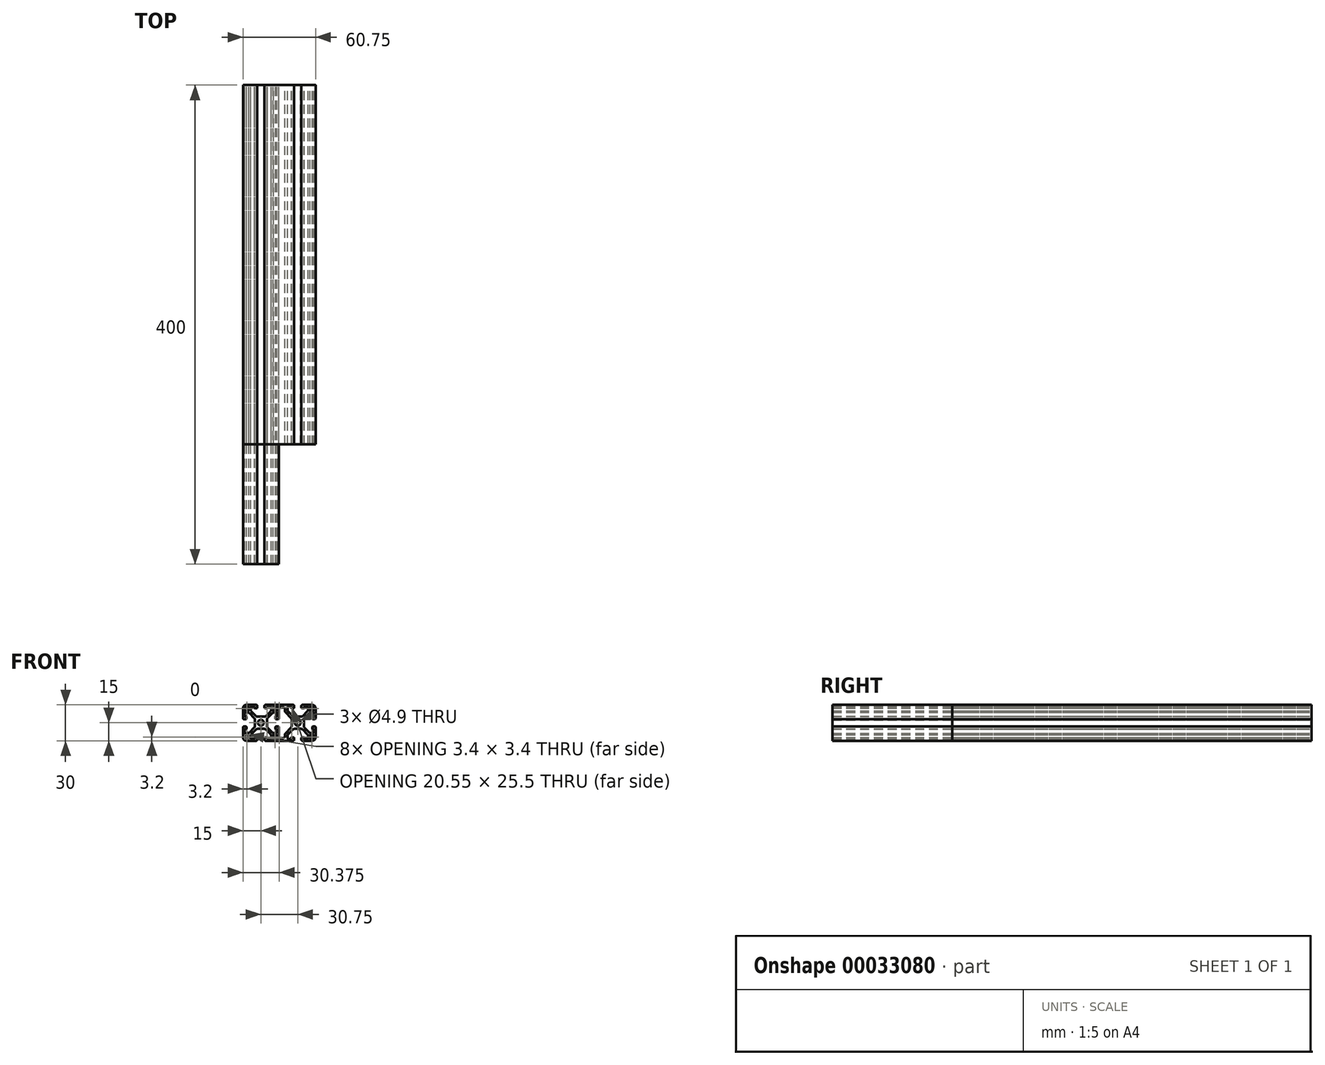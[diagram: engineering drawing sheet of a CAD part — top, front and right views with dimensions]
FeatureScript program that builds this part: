
annotation { "Feature Type Name" : "Feature", "Feature Type Description" : "" }
export const myFeature = defineFeature(function(context is Context, id is Id, definition is map)
    precondition{}
    {
        {
            var Q0;
            Q0=qCreatedBy(makeId("Front.planeOp"),FACE);
            var sketch = newSketch(context, id + "F0", { "sketchPlane" : qUnion([Q0])});
            skLineSegment(sketch, "E0.rect.bottom", {"start": v(-12, 15) * mm, "end": v(-4, 15) * mm});
            skLineSegment(sketch, "E0.rect.top", {"start": v(-12, -15) * mm, "end": v(-4, -15) * mm});
            skLineSegment(sketch, "E0.rect.left", {"start": v(-15, 12) * mm, "end": v(-15, 4) * mm});
            skLineSegment(sketch, "E0.rect.right", {"start": v(15, 12.1) * mm, "end": v(15, 4) * mm});
            skPoint(sketch, "E0.rect.middle", {"position": v(0, 0) * mm});
            skCircle(sketch, "E1", {"center": v(0, 0) * mm, "radius": 2.45 * mm});
            skLineSegment(sketch, "E2", {"start": v(-19.66, 12.1) * mm, "end": v(17.2, 12.1) * mm, "construction": true});
            skLineSegment(sketch, "E3", {"start": v(-19.97, 5.1) * mm, "end": v(17.59, 5.1) * mm, "construction": true});
            skLineSegment(sketch, "E4.rect.bottom", {"start": v(-3, 17.9) * mm, "end": v(3, 17.9) * mm, "construction": true});
            skLineSegment(sketch, "E4.rect.left", {"start": v(-3, 14) * mm, "end": v(-3, 12.85) * mm});
            skPoint(sketch, "E4.rect.middle", {"position": v(0, 15) * mm});
            skLineSegment(sketch, "E5", {"start": v(15, 15) * mm, "end": v(-15, -15) * mm, "construction": true});
            skLineSegment(sketch, "E6", {"start": v(-15, 15) * mm, "end": v(15, -15) * mm, "construction": true});
            skLineSegment(sketch, "E7", {"start": v(-9.23, 9.23) * mm, "end": v(-6.55, 6.55) * mm});
            skLineSegment(sketch, "E8", {"start": v(5.83, 5.83) * mm, "end": v(8.5, 8.5) * mm});
            skLineSegment(sketch, "E9.trimOffspring", {"start": v(4, 15) * mm, "end": v(12, 15) * mm});
            skArc(sketch, "E10.filletArc", {"start": v(-3, 14) * mm, "mid": v(-3.3, 14.7) * mm, "end": v(-4, 15) * mm});
            skPoint(sketch, "E11.visualSharp", {"position": v(8.57, 8.57) * mm});
            skPoint(sketch, "E12.visualSharp", {"position": v(-10.1, 10.1) * mm});
            skPoint(sketch, "E13.visualSharp", {"position": v(-5.1, 5.1) * mm});
            skPoint(sketch, "E14.visualSharp", {"position": v(5.1, 5.1) * mm});
            skPoint(sketch, "E15.visualSharp", {"position": v(-3, 12.1) * mm});
            skPoint(sketch, "E16.visualSharp", {"position": v(-15, 15) * mm});
            skArc(sketch, "E16.filletArc", {"start": v(-12, 15) * mm, "mid": v(-14.12, 14.12) * mm, "end": v(-15, 12) * mm});
            skPoint(sketch, "E17.MirrorP", {"position": v(10.93, 10.93) * mm});
            skPoint(sketch, "E18.MirrorP", {"position": v(10.93, 13.67) * mm});
            skPoint(sketch, "E19.MirrorP", {"position": v(13.67, 13.67) * mm});
            skPoint(sketch, "E20.MirrorP", {"position": v(13.67, 10.93) * mm});
            skPoint(sketch, "E21.newPointA", {"position": v(-3.65, 5.1) * mm});
            skPoint(sketch, "E21.newPointB", {"position": v(-5.45, 5.1) * mm});
            skLineSegment(sketch, "E22.MirrorCS", {"start": v(3, 14) * mm, "end": v(3, 12.85) * mm});
            skArc(sketch, "E23.MirrorCS", {"start": v(3, 14) * mm, "mid": v(3.3, 14.7) * mm, "end": v(4, 15) * mm});
            skLineSegment(sketch, "E24.MirrorCS", {"start": v(12, 15) * mm, "end": v(4, 15) * mm});
            skArc(sketch, "E25.MirrorCS", {"start": v(12, 15) * mm, "mid": v(14.12, 14.12) * mm, "end": v(15, 12) * mm});
            skLineSegment(sketch, "E26", {"start": v(-5.4, 13.3) * mm, "end": v(-5.4, 12.3) * mm});
            skLineSegment(sketch, "E27", {"start": v(-5.2, 12.1) * mm, "end": v(-3.75, 12.1) * mm});
            skLineSegment(sketch, "E28", {"start": v(-7.87, 9.28) * mm, "end": v(-4.42, 5.83) * mm});
            skLineSegment(sketch, "E29", {"start": v(-8.6, 11.05) * mm, "end": v(-8.6, 12.75) * mm});
            skLineSegment(sketch, "E30", {"start": v(-7.85, 13.5) * mm, "end": v(-5.6, 13.5) * mm});
            skPoint(sketch, "E31.visualSharp", {"position": v(-8.6, 10.01) * mm});
            skArc(sketch, "E31.filletArc", {"start": v(-8.6, 11.05) * mm, "mid": v(-8.4, 10.1) * mm, "end": v(-7.87, 9.28) * mm});
            skLineSegment(sketch, "E32", {"start": v(-2.65, 5.1) * mm, "end": v(0, 5.1) * mm});
            skPoint(sketch, "E33.newPointA", {"position": v(-3.69, 5.1) * mm});
            skArc(sketch, "E33.filletArc", {"start": v(-4.42, 5.83) * mm, "mid": v(-3.6, 5.3) * mm, "end": v(-2.65, 5.1) * mm});
            skPoint(sketch, "E34.visualSharp", {"position": v(-8.6, 13.5) * mm});
            skArc(sketch, "E34.filletArc", {"start": v(-7.85, 13.5) * mm, "mid": v(-8.38, 13.28) * mm, "end": v(-8.6, 12.75) * mm});
            skArc(sketch, "E35.filletArc", {"start": v(-3.75, 12.1) * mm, "mid": v(-3.22, 12.32) * mm, "end": v(-3, 12.85) * mm});
            skPoint(sketch, "E36.visualSharp", {"position": v(-5.4, 13.5) * mm});
            skArc(sketch, "E36.filletArc", {"start": v(-5.4, 13.3) * mm, "mid": v(-5.46, 13.44) * mm, "end": v(-5.6, 13.5) * mm});
            skPoint(sketch, "E37.visualSharp", {"position": v(-5.4, 12.1) * mm});
            skArc(sketch, "E37.filletArc", {"start": v(-5.4, 12.3) * mm, "mid": v(-5.34, 12.16) * mm, "end": v(-5.2, 12.1) * mm});
            skLineSegment(sketch, "E38.MirrorCS", {"start": v(2.65, 5.1) * mm, "end": v(0, 5.1) * mm});
            skArc(sketch, "E39.MirrorCS", {"start": v(4.42, 5.83) * mm, "mid": v(3.6, 5.3) * mm, "end": v(2.65, 5.1) * mm});
            skLineSegment(sketch, "E40.MirrorCS", {"start": v(7.87, 9.28) * mm, "end": v(4.42, 5.83) * mm});
            skArc(sketch, "E41.MirrorCS", {"start": v(8.6, 11.05) * mm, "mid": v(8.4, 10.1) * mm, "end": v(7.87, 9.28) * mm});
            skLineSegment(sketch, "E42.MirrorCS", {"start": v(8.6, 11.05) * mm, "end": v(8.6, 12.75) * mm});
            skArc(sketch, "E43.MirrorCS", {"start": v(7.85, 13.5) * mm, "mid": v(8.38, 13.28) * mm, "end": v(8.6, 12.75) * mm});
            skLineSegment(sketch, "E44.MirrorCS", {"start": v(7.85, 13.5) * mm, "end": v(5.6, 13.5) * mm});
            skArc(sketch, "E45.MirrorCS", {"start": v(5.4, 13.3) * mm, "mid": v(5.46, 13.44) * mm, "end": v(5.6, 13.5) * mm});
            skLineSegment(sketch, "E46.MirrorCS", {"start": v(5.4, 13.3) * mm, "end": v(5.4, 12.3) * mm});
            skArc(sketch, "E47.MirrorCS", {"start": v(5.4, 12.3) * mm, "mid": v(5.34, 12.16) * mm, "end": v(5.2, 12.1) * mm});
            skLineSegment(sketch, "E48.MirrorCS", {"start": v(5.2, 12.1) * mm, "end": v(3.75, 12.1) * mm});
            skArc(sketch, "E49.MirrorCS", {"start": v(3.75, 12.1) * mm, "mid": v(3.22, 12.32) * mm, "end": v(3, 12.85) * mm});
            skPoint(sketch, "E50.orphan", {"position": v(3, 12.1) * mm});
            skArc(sketch, "E51.MirrorCS", {"start": v(-3, -14) * mm, "mid": v(-3.3, -14.7) * mm, "end": v(-4, -15) * mm});
            skLineSegment(sketch, "E52.MirrorCS", {"start": v(-3, -14) * mm, "end": v(-3, -12.85) * mm});
            skArc(sketch, "E53.MirrorCS", {"start": v(-3.75, -12.1) * mm, "mid": v(-3.22, -12.32) * mm, "end": v(-3, -12.85) * mm});
            skLineSegment(sketch, "E54.MirrorCS", {"start": v(-5.2, -12.1) * mm, "end": v(-3.75, -12.1) * mm});
            skArc(sketch, "E55.MirrorCS", {"start": v(-5.4, -12.3) * mm, "mid": v(-5.34, -12.16) * mm, "end": v(-5.2, -12.1) * mm});
            skLineSegment(sketch, "E56.MirrorCS", {"start": v(-5.4, -13.3) * mm, "end": v(-5.4, -12.3) * mm});
            skArc(sketch, "E57.MirrorCS", {"start": v(-5.4, -13.3) * mm, "mid": v(-5.46, -13.44) * mm, "end": v(-5.6, -13.5) * mm});
            skLineSegment(sketch, "E58.MirrorCS", {"start": v(-7.85, -13.5) * mm, "end": v(-5.6, -13.5) * mm});
            skArc(sketch, "E59.MirrorCS", {"start": v(-7.85, -13.5) * mm, "mid": v(-8.38, -13.28) * mm, "end": v(-8.6, -12.75) * mm});
            skLineSegment(sketch, "E60.MirrorCS", {"start": v(-8.6, -11.05) * mm, "end": v(-8.6, -12.75) * mm});
            skArc(sketch, "E61.MirrorCS", {"start": v(-8.6, -11.05) * mm, "mid": v(-8.4, -10.1) * mm, "end": v(-7.87, -9.28) * mm});
            skLineSegment(sketch, "E62.MirrorCS", {"start": v(-7.87, -9.28) * mm, "end": v(-4.42, -5.83) * mm});
            skArc(sketch, "E63.MirrorCS", {"start": v(-4.42, -5.83) * mm, "mid": v(-3.6, -5.3) * mm, "end": v(-2.65, -5.1) * mm});
            skLineSegment(sketch, "E64.MirrorCS", {"start": v(-2.65, -5.1) * mm, "end": v(0, -5.1) * mm});
            skLineSegment(sketch, "E65.MirrorCS", {"start": v(2.65, -5.1) * mm, "end": v(0, -5.1) * mm});
            skArc(sketch, "E66.MirrorCS", {"start": v(4.42, -5.83) * mm, "mid": v(3.6, -5.3) * mm, "end": v(2.65, -5.1) * mm});
            skLineSegment(sketch, "E67.MirrorCS", {"start": v(7.87, -9.28) * mm, "end": v(4.42, -5.83) * mm});
            skArc(sketch, "E68.MirrorCS", {"start": v(8.6, -11.05) * mm, "mid": v(8.4, -10.1) * mm, "end": v(7.87, -9.28) * mm});
            skLineSegment(sketch, "E69.MirrorCS", {"start": v(8.6, -11.05) * mm, "end": v(8.6, -12.75) * mm});
            skArc(sketch, "E70.MirrorCS", {"start": v(7.85, -13.5) * mm, "mid": v(8.38, -13.28) * mm, "end": v(8.6, -12.75) * mm});
            skLineSegment(sketch, "E71.MirrorCS", {"start": v(7.85, -13.5) * mm, "end": v(5.6, -13.5) * mm});
            skArc(sketch, "E72.MirrorCS", {"start": v(5.4, -13.3) * mm, "mid": v(5.46, -13.44) * mm, "end": v(5.6, -13.5) * mm});
            skLineSegment(sketch, "E73.MirrorCS", {"start": v(5.4, -13.3) * mm, "end": v(5.4, -12.3) * mm});
            skArc(sketch, "E74.MirrorCS", {"start": v(5.4, -12.3) * mm, "mid": v(5.34, -12.16) * mm, "end": v(5.2, -12.1) * mm});
            skLineSegment(sketch, "E75.MirrorCS", {"start": v(5.2, -12.1) * mm, "end": v(3.75, -12.1) * mm});
            skArc(sketch, "E76.MirrorCS", {"start": v(3.75, -12.1) * mm, "mid": v(3.22, -12.32) * mm, "end": v(3, -12.85) * mm});
            skLineSegment(sketch, "E77.MirrorCS", {"start": v(3, -14) * mm, "end": v(3, -12.85) * mm});
            skArc(sketch, "E78.MirrorCS", {"start": v(3, -14) * mm, "mid": v(3.3, -14.7) * mm, "end": v(4, -15) * mm});
            skArc(sketch, "E79.MirrorCS", {"start": v(12, -15) * mm, "mid": v(14.12, -14.12) * mm, "end": v(15, -12) * mm});
            skArc(sketch, "E80.MirrorCS", {"start": v(-12, -15) * mm, "mid": v(-14.12, -14.12) * mm, "end": v(-15, -12) * mm});
            skArc(sketch, "E81.MirrorCS", {"start": v(14, 3) * mm, "mid": v(14.7, 3.3) * mm, "end": v(15, 4) * mm});
            skLineSegment(sketch, "E82.MirrorCS", {"start": v(14, 3) * mm, "end": v(12.85, 3) * mm});
            skArc(sketch, "E83.MirrorCS", {"start": v(12.1, 3.75) * mm, "mid": v(12.32, 3.22) * mm, "end": v(12.85, 3) * mm});
            skLineSegment(sketch, "E84.MirrorCS", {"start": v(12.1, 5.2) * mm, "end": v(12.1, 3.75) * mm});
            skArc(sketch, "E85.MirrorCS", {"start": v(12.3, 5.4) * mm, "mid": v(12.16, 5.34) * mm, "end": v(12.1, 5.2) * mm});
            skLineSegment(sketch, "E86.MirrorCS", {"start": v(13.3, 5.4) * mm, "end": v(12.3, 5.4) * mm});
            skArc(sketch, "E87.MirrorCS", {"start": v(13.3, 5.4) * mm, "mid": v(13.44, 5.46) * mm, "end": v(13.5, 5.6) * mm});
            skLineSegment(sketch, "E88.MirrorCS", {"start": v(13.5, 7.85) * mm, "end": v(13.5, 5.6) * mm});
            skArc(sketch, "E89.MirrorCS", {"start": v(13.5, 7.85) * mm, "mid": v(13.28, 8.38) * mm, "end": v(12.75, 8.6) * mm});
            skLineSegment(sketch, "E90.MirrorCS", {"start": v(11.05, 8.6) * mm, "end": v(12.75, 8.6) * mm});
            skArc(sketch, "E91.MirrorCS", {"start": v(11.05, 8.6) * mm, "mid": v(10.1, 8.4) * mm, "end": v(9.28, 7.87) * mm});
            skLineSegment(sketch, "E92.MirrorCS", {"start": v(9.28, 7.87) * mm, "end": v(5.83, 4.42) * mm});
            skArc(sketch, "E93.MirrorCS", {"start": v(5.83, 4.42) * mm, "mid": v(5.3, 3.6) * mm, "end": v(5.1, 2.65) * mm});
            skLineSegment(sketch, "E94.MirrorCS", {"start": v(5.1, 2.65) * mm, "end": v(5.1, 0) * mm});
            skLineSegment(sketch, "E95.MirrorCS", {"start": v(5.1, -2.65) * mm, "end": v(5.1, 0) * mm});
            skArc(sketch, "E96.MirrorCS", {"start": v(5.83, -4.42) * mm, "mid": v(5.3, -3.6) * mm, "end": v(5.1, -2.65) * mm});
            skLineSegment(sketch, "E97.MirrorCS", {"start": v(9.28, -7.87) * mm, "end": v(5.83, -4.42) * mm});
            skArc(sketch, "E98.MirrorCS", {"start": v(11.05, -8.6) * mm, "mid": v(10.1, -8.4) * mm, "end": v(9.28, -7.87) * mm});
            skLineSegment(sketch, "E99.MirrorCS", {"start": v(11.05, -8.6) * mm, "end": v(12.75, -8.6) * mm});
            skArc(sketch, "E100.MirrorCS", {"start": v(13.5, -7.85) * mm, "mid": v(13.28, -8.38) * mm, "end": v(12.75, -8.6) * mm});
            skLineSegment(sketch, "E101.MirrorCS", {"start": v(13.5, -7.85) * mm, "end": v(13.5, -5.6) * mm});
            skArc(sketch, "E102.MirrorCS", {"start": v(13.3, -5.4) * mm, "mid": v(13.44, -5.46) * mm, "end": v(13.5, -5.6) * mm});
            skLineSegment(sketch, "E103.MirrorCS", {"start": v(13.3, -5.4) * mm, "end": v(12.3, -5.4) * mm});
            skArc(sketch, "E104.MirrorCS", {"start": v(12.3, -5.4) * mm, "mid": v(12.16, -5.34) * mm, "end": v(12.1, -5.2) * mm});
            skLineSegment(sketch, "E105.MirrorCS", {"start": v(12.1, -5.2) * mm, "end": v(12.1, -3.75) * mm});
            skArc(sketch, "E106.MirrorCS", {"start": v(12.1, -3.75) * mm, "mid": v(12.32, -3.22) * mm, "end": v(12.85, -3) * mm});
            skLineSegment(sketch, "E107.MirrorCS", {"start": v(14, -3) * mm, "end": v(12.85, -3) * mm});
            skArc(sketch, "E108.MirrorCS", {"start": v(14, -3) * mm, "mid": v(14.7, -3.3) * mm, "end": v(15, -4) * mm});
            skArc(sketch, "E109.MirrorCS", {"start": v(-14, 3) * mm, "mid": v(-14.7, 3.3) * mm, "end": v(-15, 4) * mm});
            skLineSegment(sketch, "E110.MirrorCS", {"start": v(-14, 3) * mm, "end": v(-12.85, 3) * mm});
            skArc(sketch, "E111.MirrorCS", {"start": v(-12.1, 3.75) * mm, "mid": v(-12.32, 3.22) * mm, "end": v(-12.85, 3) * mm});
            skLineSegment(sketch, "E112.MirrorCS", {"start": v(-12.1, 5.2) * mm, "end": v(-12.1, 3.75) * mm});
            skArc(sketch, "E113.MirrorCS", {"start": v(-12.3, 5.4) * mm, "mid": v(-12.16, 5.34) * mm, "end": v(-12.1, 5.2) * mm});
            skLineSegment(sketch, "E114.MirrorCS", {"start": v(-13.3, 5.4) * mm, "end": v(-12.3, 5.4) * mm});
            skArc(sketch, "E115.MirrorCS", {"start": v(-13.3, 5.4) * mm, "mid": v(-13.44, 5.46) * mm, "end": v(-13.5, 5.6) * mm});
            skLineSegment(sketch, "E116.MirrorCS", {"start": v(-13.5, 7.85) * mm, "end": v(-13.5, 5.6) * mm});
            skArc(sketch, "E117.MirrorCS", {"start": v(-13.5, 7.85) * mm, "mid": v(-13.28, 8.38) * mm, "end": v(-12.75, 8.6) * mm});
            skLineSegment(sketch, "E118.MirrorCS", {"start": v(-11.05, 8.6) * mm, "end": v(-12.75, 8.6) * mm});
            skArc(sketch, "E119.MirrorCS", {"start": v(-11.05, 8.6) * mm, "mid": v(-10.1, 8.4) * mm, "end": v(-9.28, 7.87) * mm});
            skLineSegment(sketch, "E120.MirrorCS", {"start": v(-9.28, 7.87) * mm, "end": v(-5.83, 4.42) * mm});
            skArc(sketch, "E121.MirrorCS", {"start": v(-5.83, 4.42) * mm, "mid": v(-5.3, 3.6) * mm, "end": v(-5.1, 2.65) * mm});
            skLineSegment(sketch, "E122.MirrorCS", {"start": v(-5.1, 2.65) * mm, "end": v(-5.1, 0) * mm});
            skLineSegment(sketch, "E123.MirrorCS", {"start": v(-5.1, -2.65) * mm, "end": v(-5.1, 0) * mm});
            skArc(sketch, "E124.MirrorCS", {"start": v(-5.83, -4.42) * mm, "mid": v(-5.3, -3.6) * mm, "end": v(-5.1, -2.65) * mm});
            skLineSegment(sketch, "E125.MirrorCS", {"start": v(-9.28, -7.87) * mm, "end": v(-5.83, -4.42) * mm});
            skArc(sketch, "E126.MirrorCS", {"start": v(-11.05, -8.6) * mm, "mid": v(-10.1, -8.4) * mm, "end": v(-9.28, -7.87) * mm});
            skLineSegment(sketch, "E127.MirrorCS", {"start": v(-11.05, -8.6) * mm, "end": v(-12.75, -8.6) * mm});
            skArc(sketch, "E128.MirrorCS", {"start": v(-13.5, -7.85) * mm, "mid": v(-13.28, -8.38) * mm, "end": v(-12.75, -8.6) * mm});
            skLineSegment(sketch, "E129.MirrorCS", {"start": v(-13.5, -7.85) * mm, "end": v(-13.5, -5.6) * mm});
            skArc(sketch, "E130.MirrorCS", {"start": v(-13.3, -5.4) * mm, "mid": v(-13.44, -5.46) * mm, "end": v(-13.5, -5.6) * mm});
            skLineSegment(sketch, "E131.MirrorCS", {"start": v(-13.3, -5.4) * mm, "end": v(-12.3, -5.4) * mm});
            skArc(sketch, "E132.MirrorCS", {"start": v(-12.3, -5.4) * mm, "mid": v(-12.16, -5.34) * mm, "end": v(-12.1, -5.2) * mm});
            skLineSegment(sketch, "E133.MirrorCS", {"start": v(-12.1, -5.2) * mm, "end": v(-12.1, -3.75) * mm});
            skArc(sketch, "E134.MirrorCS", {"start": v(-12.1, -3.75) * mm, "mid": v(-12.32, -3.22) * mm, "end": v(-12.85, -3) * mm});
            skLineSegment(sketch, "E135.MirrorCS", {"start": v(-14, -3) * mm, "end": v(-12.85, -3) * mm});
            skArc(sketch, "E136.MirrorCS", {"start": v(-14, -3) * mm, "mid": v(-14.7, -3.3) * mm, "end": v(-15, -4) * mm});
            skLineSegment(sketch, "E137.trimOffspring", {"start": v(15, -4) * mm, "end": v(15, -12) * mm});
            skLineSegment(sketch, "E138.trimOffspring", {"start": v(-15, -4) * mm, "end": v(-15, -12) * mm});
            skLineSegment(sketch, "E139.trimOffspring", {"start": v(4, -15) * mm, "end": v(12, -15) * mm});
            skLineSegment(sketch, "E140.bottom", {"start": v(-12, 13.5) * mm, "end": v(-10.3, 13.5) * mm});
            skLineSegment(sketch, "E140.top", {"start": v(-13.3, 10.1) * mm, "end": v(-10.3, 10.1) * mm});
            skLineSegment(sketch, "E140.left", {"start": v(-13.5, 12) * mm, "end": v(-13.5, 10.3) * mm});
            skLineSegment(sketch, "E140.right", {"start": v(-10.1, 13.3) * mm, "end": v(-10.1, 10.3) * mm});
            skPoint(sketch, "E141.visualSharp", {"position": v(-13.5, 13.5) * mm});
            skArc(sketch, "E141.filletArc", {"start": v(-12, 13.5) * mm, "mid": v(-13.06, 13.06) * mm, "end": v(-13.5, 12) * mm});
            skPoint(sketch, "E142.visualSharp", {"position": v(-10.1, 13.5) * mm});
            skArc(sketch, "E142.filletArc", {"start": v(-10.1, 13.3) * mm, "mid": v(-10.16, 13.44) * mm, "end": v(-10.3, 13.5) * mm});
            skArc(sketch, "E143.filletArc", {"start": v(-10.3, 10.1) * mm, "mid": v(-10.16, 10.16) * mm, "end": v(-10.1, 10.3) * mm});
            skPoint(sketch, "E144.visualSharp", {"position": v(-13.5, 10.1) * mm});
            skArc(sketch, "E144.filletArc", {"start": v(-13.5, 10.3) * mm, "mid": v(-13.44, 10.16) * mm, "end": v(-13.3, 10.1) * mm});
            skLineSegment(sketch, "E145.MirrorCS", {"start": v(10.1, 13.3) * mm, "end": v(10.1, 10.3) * mm});
            skArc(sketch, "E146.MirrorCS", {"start": v(10.1, 13.3) * mm, "mid": v(10.16, 13.44) * mm, "end": v(10.3, 13.5) * mm});
            skLineSegment(sketch, "E147.MirrorCS", {"start": v(12, 13.5) * mm, "end": v(10.3, 13.5) * mm});
            skArc(sketch, "E148.MirrorCS", {"start": v(12, 13.5) * mm, "mid": v(13.06, 13.06) * mm, "end": v(13.5, 12) * mm});
            skLineSegment(sketch, "E149.MirrorCS", {"start": v(13.5, 12) * mm, "end": v(13.5, 10.3) * mm});
            skArc(sketch, "E150.MirrorCS", {"start": v(13.5, 10.3) * mm, "mid": v(13.44, 10.16) * mm, "end": v(13.3, 10.1) * mm});
            skLineSegment(sketch, "E151.MirrorCS", {"start": v(13.3, 10.1) * mm, "end": v(10.3, 10.1) * mm});
            skArc(sketch, "E152.MirrorCS", {"start": v(10.3, 10.1) * mm, "mid": v(10.16, 10.16) * mm, "end": v(10.1, 10.3) * mm});
            skLineSegment(sketch, "E153.MirrorCS", {"start": v(-10.1, -13.3) * mm, "end": v(-10.1, -10.3) * mm});
            skArc(sketch, "E154.MirrorCS", {"start": v(-10.1, -13.3) * mm, "mid": v(-10.16, -13.44) * mm, "end": v(-10.3, -13.5) * mm});
            skLineSegment(sketch, "E155.MirrorCS", {"start": v(-12, -13.5) * mm, "end": v(-10.3, -13.5) * mm});
            skArc(sketch, "E156.MirrorCS", {"start": v(-12, -13.5) * mm, "mid": v(-13.06, -13.06) * mm, "end": v(-13.5, -12) * mm});
            skLineSegment(sketch, "E157.MirrorCS", {"start": v(-13.5, -12) * mm, "end": v(-13.5, -10.3) * mm});
            skArc(sketch, "E158.MirrorCS", {"start": v(-13.5, -10.3) * mm, "mid": v(-13.44, -10.16) * mm, "end": v(-13.3, -10.1) * mm});
            skLineSegment(sketch, "E159.MirrorCS", {"start": v(-13.3, -10.1) * mm, "end": v(-10.3, -10.1) * mm});
            skArc(sketch, "E160.MirrorCS", {"start": v(-10.3, -10.1) * mm, "mid": v(-10.16, -10.16) * mm, "end": v(-10.1, -10.3) * mm});
            skLineSegment(sketch, "E161.MirrorCS", {"start": v(10.1, -13.3) * mm, "end": v(10.1, -10.3) * mm});
            skArc(sketch, "E162.MirrorCS", {"start": v(10.3, -10.1) * mm, "mid": v(10.16, -10.16) * mm, "end": v(10.1, -10.3) * mm});
            skLineSegment(sketch, "E163.MirrorCS", {"start": v(13.3, -10.1) * mm, "end": v(10.3, -10.1) * mm});
            skArc(sketch, "E164.MirrorCS", {"start": v(13.5, -10.3) * mm, "mid": v(13.44, -10.16) * mm, "end": v(13.3, -10.1) * mm});
            skLineSegment(sketch, "E165.MirrorCS", {"start": v(13.5, -12) * mm, "end": v(13.5, -10.3) * mm});
            skArc(sketch, "E166.MirrorCS", {"start": v(12, -13.5) * mm, "mid": v(13.06, -13.06) * mm, "end": v(13.5, -12) * mm});
            skLineSegment(sketch, "E167.MirrorCS", {"start": v(12, -13.5) * mm, "end": v(10.3, -13.5) * mm});
            skArc(sketch, "E168.MirrorCS", {"start": v(10.1, -13.3) * mm, "mid": v(10.16, -13.44) * mm, "end": v(10.3, -13.5) * mm});
            skSolve(sketch);
        }
        {
            var Q0;
            Q0=makeQuery(id+"F0.imprint","IMPRINT",FACE,{"disambiguationData":[TD([[makeQuery(id+"F0.imprint","IMPRINT",EDGE,{"derivedFrom":sQuery(id+"F0.wireOp",EDGE,"E0.rect.bottom")}),-1.0]])]});
            extrude(context, id + "F1", {"entities" : qUnion([Q0]), "depth" : 400 * mm});
        }
        {
            var Q0;
            Q0=qCreatedBy(makeId("Front.planeOp"),FACE);
            var sketch = newSketch(context, id + "F2", { "sketchPlane" : qUnion([Q0])});
            skCircle(sketch, "E169.0", {"center": v(0, 0) * mm, "radius": 2.45 * mm});
            skLineSegment(sketch, "E170.0.0", {"start": v(-4, 15) * mm, "end": v(-12, 15) * mm});
            skArc(sketch, "E170.0.1", {"start": v(-12, 15) * mm, "mid": v(-14.12, 14.12) * mm, "end": v(-15, 12) * mm});
            skLineSegment(sketch, "E170.0.2", {"start": v(-15, 12) * mm, "end": v(-15, 4) * mm});
            skArc(sketch, "E170.0.3", {"start": v(-15, 4) * mm, "mid": v(-14.7, 3.3) * mm, "end": v(-14, 3) * mm});
            skLineSegment(sketch, "E170.0.4", {"start": v(-14, 3) * mm, "end": v(-12.85, 3) * mm});
            skArc(sketch, "E170.0.5", {"start": v(-12.85, 3) * mm, "mid": v(-12.32, 3.22) * mm, "end": v(-12.1, 3.75) * mm});
            skLineSegment(sketch, "E170.0.6", {"start": v(-12.1, 3.75) * mm, "end": v(-12.1, 5.2) * mm});
            skArc(sketch, "E170.0.7", {"start": v(-12.1, 5.2) * mm, "mid": v(-12.16, 5.34) * mm, "end": v(-12.3, 5.4) * mm});
            skLineSegment(sketch, "E170.0.8", {"start": v(-12.3, 5.4) * mm, "end": v(-13.3, 5.4) * mm});
            skArc(sketch, "E170.0.9", {"start": v(-13.3, 5.4) * mm, "mid": v(-13.44, 5.46) * mm, "end": v(-13.5, 5.6) * mm});
            skLineSegment(sketch, "E170.0.10", {"start": v(-13.5, 5.6) * mm, "end": v(-13.5, 7.85) * mm});
            skArc(sketch, "E170.0.11", {"start": v(-13.5, 7.85) * mm, "mid": v(-13.28, 8.38) * mm, "end": v(-12.75, 8.6) * mm});
            skLineSegment(sketch, "E170.0.12", {"start": v(-12.75, 8.6) * mm, "end": v(-11.05, 8.6) * mm});
            skArc(sketch, "E170.0.13", {"start": v(-11.05, 8.6) * mm, "mid": v(-10.1, 8.4) * mm, "end": v(-9.28, 7.87) * mm});
            skLineSegment(sketch, "E170.0.14", {"start": v(-9.28, 7.87) * mm, "end": v(-5.83, 4.42) * mm});
            skArc(sketch, "E170.0.15", {"start": v(-5.83, 4.42) * mm, "mid": v(-5.3, 3.6) * mm, "end": v(-5.1, 2.65) * mm});
            skLineSegment(sketch, "E170.0.16", {"start": v(-5.1, 2.65) * mm, "end": v(-5.1, 0) * mm});
            skLineSegment(sketch, "E170.0.17", {"start": v(-5.1, 0) * mm, "end": v(-5.1, -2.65) * mm});
            skArc(sketch, "E170.0.18", {"start": v(-5.1, -2.65) * mm, "mid": v(-5.3, -3.6) * mm, "end": v(-5.83, -4.42) * mm});
            skLineSegment(sketch, "E170.0.19", {"start": v(-5.83, -4.42) * mm, "end": v(-9.28, -7.87) * mm});
            skArc(sketch, "E170.0.20", {"start": v(-9.28, -7.87) * mm, "mid": v(-10.1, -8.4) * mm, "end": v(-11.05, -8.6) * mm});
            skLineSegment(sketch, "E170.0.21", {"start": v(-11.05, -8.6) * mm, "end": v(-12.75, -8.6) * mm});
            skArc(sketch, "E170.0.22", {"start": v(-12.75, -8.6) * mm, "mid": v(-13.28, -8.38) * mm, "end": v(-13.5, -7.85) * mm});
            skLineSegment(sketch, "E170.0.23", {"start": v(-13.5, -7.85) * mm, "end": v(-13.5, -5.6) * mm});
            skArc(sketch, "E170.0.24", {"start": v(-13.5, -5.6) * mm, "mid": v(-13.44, -5.46) * mm, "end": v(-13.3, -5.4) * mm});
            skLineSegment(sketch, "E170.0.25", {"start": v(-13.3, -5.4) * mm, "end": v(-12.3, -5.4) * mm});
            skArc(sketch, "E170.0.26", {"start": v(-12.3, -5.4) * mm, "mid": v(-12.16, -5.34) * mm, "end": v(-12.1, -5.2) * mm});
            skLineSegment(sketch, "E170.0.27", {"start": v(-12.1, -5.2) * mm, "end": v(-12.1, -3.75) * mm});
            skArc(sketch, "E170.0.28", {"start": v(-12.1, -3.75) * mm, "mid": v(-12.32, -3.22) * mm, "end": v(-12.85, -3) * mm});
            skLineSegment(sketch, "E170.0.29", {"start": v(-12.85, -3) * mm, "end": v(-14, -3) * mm});
            skArc(sketch, "E170.0.30", {"start": v(-14, -3) * mm, "mid": v(-14.7, -3.3) * mm, "end": v(-15, -4) * mm});
            skLineSegment(sketch, "E170.0.31", {"start": v(-15, -4) * mm, "end": v(-15, -12) * mm});
            skArc(sketch, "E170.0.32", {"start": v(-15, -12) * mm, "mid": v(-14.12, -14.12) * mm, "end": v(-12, -15) * mm});
            skLineSegment(sketch, "E170.0.33", {"start": v(-12, -15) * mm, "end": v(-4, -15) * mm});
            skArc(sketch, "E170.0.34", {"start": v(-4, -15) * mm, "mid": v(-3.3, -14.7) * mm, "end": v(-3, -14) * mm});
            skLineSegment(sketch, "E170.0.35", {"start": v(-3, -14) * mm, "end": v(-3, -12.85) * mm});
            skArc(sketch, "E170.0.36", {"start": v(-3, -12.85) * mm, "mid": v(-3.22, -12.32) * mm, "end": v(-3.75, -12.1) * mm});
            skLineSegment(sketch, "E170.0.37", {"start": v(-3.75, -12.1) * mm, "end": v(-5.2, -12.1) * mm});
            skArc(sketch, "E170.0.38", {"start": v(-5.2, -12.1) * mm, "mid": v(-5.34, -12.16) * mm, "end": v(-5.4, -12.3) * mm});
            skLineSegment(sketch, "E170.0.39", {"start": v(-5.4, -12.3) * mm, "end": v(-5.4, -13.3) * mm});
            skArc(sketch, "E170.0.40", {"start": v(-5.4, -13.3) * mm, "mid": v(-5.46, -13.44) * mm, "end": v(-5.6, -13.5) * mm});
            skLineSegment(sketch, "E170.0.41", {"start": v(-5.6, -13.5) * mm, "end": v(-7.85, -13.5) * mm});
            skArc(sketch, "E170.0.42", {"start": v(-7.85, -13.5) * mm, "mid": v(-8.38, -13.28) * mm, "end": v(-8.6, -12.75) * mm});
            skLineSegment(sketch, "E170.0.43", {"start": v(-8.6, -12.75) * mm, "end": v(-8.6, -11.05) * mm});
            skArc(sketch, "E170.0.44", {"start": v(-8.6, -11.05) * mm, "mid": v(-8.4, -10.1) * mm, "end": v(-7.87, -9.28) * mm});
            skLineSegment(sketch, "E170.0.45", {"start": v(-7.87, -9.28) * mm, "end": v(-4.42, -5.83) * mm});
            skArc(sketch, "E170.0.46", {"start": v(-4.42, -5.83) * mm, "mid": v(-3.6, -5.3) * mm, "end": v(-2.65, -5.1) * mm});
            skLineSegment(sketch, "E170.0.47", {"start": v(-2.65, -5.1) * mm, "end": v(0, -5.1) * mm});
            skLineSegment(sketch, "E170.0.48", {"start": v(0, -5.1) * mm, "end": v(2.65, -5.1) * mm});
            skArc(sketch, "E170.0.49", {"start": v(2.65, -5.1) * mm, "mid": v(3.6, -5.3) * mm, "end": v(4.42, -5.83) * mm});
            skLineSegment(sketch, "E170.0.50", {"start": v(4.42, -5.83) * mm, "end": v(7.87, -9.28) * mm});
            skArc(sketch, "E170.0.51", {"start": v(7.87, -9.28) * mm, "mid": v(8.4, -10.1) * mm, "end": v(8.6, -11.05) * mm});
            skLineSegment(sketch, "E170.0.52", {"start": v(8.6, -11.05) * mm, "end": v(8.6, -12.75) * mm});
            skArc(sketch, "E170.0.53", {"start": v(8.6, -12.75) * mm, "mid": v(8.38, -13.28) * mm, "end": v(7.85, -13.5) * mm});
            skLineSegment(sketch, "E170.0.54", {"start": v(7.85, -13.5) * mm, "end": v(5.6, -13.5) * mm});
            skArc(sketch, "E170.0.55", {"start": v(5.6, -13.5) * mm, "mid": v(5.46, -13.44) * mm, "end": v(5.4, -13.3) * mm});
            skLineSegment(sketch, "E170.0.56", {"start": v(5.4, -13.3) * mm, "end": v(5.4, -12.3) * mm});
            skArc(sketch, "E170.0.57", {"start": v(5.4, -12.3) * mm, "mid": v(5.34, -12.16) * mm, "end": v(5.2, -12.1) * mm});
            skLineSegment(sketch, "E170.0.58", {"start": v(5.2, -12.1) * mm, "end": v(3.75, -12.1) * mm});
            skArc(sketch, "E170.0.59", {"start": v(3.75, -12.1) * mm, "mid": v(3.22, -12.32) * mm, "end": v(3, -12.85) * mm});
            skLineSegment(sketch, "E170.0.60", {"start": v(3, -12.85) * mm, "end": v(3, -14) * mm});
            skArc(sketch, "E170.0.61", {"start": v(3, -14) * mm, "mid": v(3.3, -14.7) * mm, "end": v(4, -15) * mm});
            skLineSegment(sketch, "E170.0.76", {"start": v(9.28, -7.87) * mm, "end": v(5.83, -4.42) * mm});
            skArc(sketch, "E170.0.77", {"start": v(5.83, -4.42) * mm, "mid": v(5.3, -3.6) * mm, "end": v(5.1, -2.65) * mm});
            skLineSegment(sketch, "E170.0.78", {"start": v(5.1, -2.65) * mm, "end": v(5.1, 0) * mm});
            skLineSegment(sketch, "E170.0.79", {"start": v(5.1, 0) * mm, "end": v(5.1, 2.65) * mm});
            skArc(sketch, "E170.0.80", {"start": v(5.1, 2.65) * mm, "mid": v(5.3, 3.6) * mm, "end": v(5.83, 4.42) * mm});
            skLineSegment(sketch, "E170.0.81", {"start": v(5.83, 4.42) * mm, "end": v(9.28, 7.87) * mm});
            skArc(sketch, "E170.0.96", {"start": v(4, 15) * mm, "mid": v(3.3, 14.7) * mm, "end": v(3, 14) * mm});
            skLineSegment(sketch, "E170.0.97", {"start": v(3, 14) * mm, "end": v(3, 12.85) * mm});
            skArc(sketch, "E170.0.98", {"start": v(3, 12.85) * mm, "mid": v(3.22, 12.32) * mm, "end": v(3.75, 12.1) * mm});
            skLineSegment(sketch, "E170.0.99", {"start": v(3.75, 12.1) * mm, "end": v(5.2, 12.1) * mm});
            skArc(sketch, "E170.0.100", {"start": v(5.2, 12.1) * mm, "mid": v(5.34, 12.16) * mm, "end": v(5.4, 12.3) * mm});
            skLineSegment(sketch, "E170.0.101", {"start": v(5.4, 12.3) * mm, "end": v(5.4, 13.3) * mm});
            skArc(sketch, "E170.0.102", {"start": v(5.4, 13.3) * mm, "mid": v(5.46, 13.44) * mm, "end": v(5.6, 13.5) * mm});
            skLineSegment(sketch, "E170.0.103", {"start": v(5.6, 13.5) * mm, "end": v(7.85, 13.5) * mm});
            skArc(sketch, "E170.0.104", {"start": v(7.85, 13.5) * mm, "mid": v(8.38, 13.28) * mm, "end": v(8.6, 12.75) * mm});
            skLineSegment(sketch, "E170.0.105", {"start": v(8.6, 12.75) * mm, "end": v(8.6, 11.05) * mm});
            skArc(sketch, "E170.0.106", {"start": v(8.6, 11.05) * mm, "mid": v(8.4, 10.1) * mm, "end": v(7.87, 9.28) * mm});
            skLineSegment(sketch, "E170.0.107", {"start": v(7.87, 9.28) * mm, "end": v(4.42, 5.83) * mm});
            skArc(sketch, "E170.0.108", {"start": v(4.42, 5.83) * mm, "mid": v(3.6, 5.3) * mm, "end": v(2.65, 5.1) * mm});
            skLineSegment(sketch, "E170.0.109", {"start": v(2.65, 5.1) * mm, "end": v(0, 5.1) * mm});
            skLineSegment(sketch, "E170.0.110", {"start": v(0, 5.1) * mm, "end": v(-2.65, 5.1) * mm});
            skArc(sketch, "E170.0.111", {"start": v(-2.65, 5.1) * mm, "mid": v(-3.6, 5.3) * mm, "end": v(-4.42, 5.83) * mm});
            skLineSegment(sketch, "E170.0.112", {"start": v(-4.42, 5.83) * mm, "end": v(-7.87, 9.28) * mm});
            skArc(sketch, "E170.0.113", {"start": v(-7.87, 9.28) * mm, "mid": v(-8.4, 10.1) * mm, "end": v(-8.6, 11.05) * mm});
            skLineSegment(sketch, "E170.0.114", {"start": v(-8.6, 11.05) * mm, "end": v(-8.6, 12.75) * mm});
            skArc(sketch, "E170.0.115", {"start": v(-8.6, 12.75) * mm, "mid": v(-8.38, 13.28) * mm, "end": v(-7.85, 13.5) * mm});
            skLineSegment(sketch, "E170.0.116", {"start": v(-7.85, 13.5) * mm, "end": v(-5.6, 13.5) * mm});
            skArc(sketch, "E170.0.117", {"start": v(-5.6, 13.5) * mm, "mid": v(-5.46, 13.44) * mm, "end": v(-5.4, 13.3) * mm});
            skLineSegment(sketch, "E170.0.118", {"start": v(-5.4, 13.3) * mm, "end": v(-5.4, 12.3) * mm});
            skArc(sketch, "E170.0.119", {"start": v(-5.4, 12.3) * mm, "mid": v(-5.34, 12.16) * mm, "end": v(-5.2, 12.1) * mm});
            skLineSegment(sketch, "E170.0.120", {"start": v(-5.2, 12.1) * mm, "end": v(-3.75, 12.1) * mm});
            skArc(sketch, "E170.0.121", {"start": v(-3.75, 12.1) * mm, "mid": v(-3.22, 12.32) * mm, "end": v(-3, 12.85) * mm});
            skLineSegment(sketch, "E170.0.122", {"start": v(-3, 12.85) * mm, "end": v(-3, 14) * mm});
            skArc(sketch, "E170.0.123", {"start": v(-3, 14) * mm, "mid": v(-3.3, 14.7) * mm, "end": v(-4, 15) * mm});
            skLineSegment(sketch, "E171.0.0", {"start": v(-10.3, 13.5) * mm, "end": v(-12, 13.5) * mm});
            skArc(sketch, "E171.0.1", {"start": v(-12, 13.5) * mm, "mid": v(-13.06, 13.06) * mm, "end": v(-13.5, 12) * mm});
            skLineSegment(sketch, "E171.0.2", {"start": v(-13.5, 12) * mm, "end": v(-13.5, 10.3) * mm});
            skArc(sketch, "E171.0.3", {"start": v(-13.5, 10.3) * mm, "mid": v(-13.44, 10.16) * mm, "end": v(-13.3, 10.1) * mm});
            skLineSegment(sketch, "E171.0.4", {"start": v(-13.3, 10.1) * mm, "end": v(-10.3, 10.1) * mm});
            skArc(sketch, "E171.0.5", {"start": v(-10.3, 10.1) * mm, "mid": v(-10.16, 10.16) * mm, "end": v(-10.1, 10.3) * mm});
            skLineSegment(sketch, "E171.0.6", {"start": v(-10.1, 10.3) * mm, "end": v(-10.1, 13.3) * mm});
            skArc(sketch, "E171.0.7", {"start": v(-10.1, 13.3) * mm, "mid": v(-10.16, 13.44) * mm, "end": v(-10.3, 13.5) * mm});
            skArc(sketch, "E172.0.0", {"start": v(-10.3, -13.5) * mm, "mid": v(-10.16, -13.44) * mm, "end": v(-10.1, -13.3) * mm});
            skLineSegment(sketch, "E172.0.1", {"start": v(-10.1, -13.3) * mm, "end": v(-10.1, -10.3) * mm});
            skArc(sketch, "E172.0.2", {"start": v(-10.1, -10.3) * mm, "mid": v(-10.16, -10.16) * mm, "end": v(-10.3, -10.1) * mm});
            skLineSegment(sketch, "E172.0.3", {"start": v(-10.3, -10.1) * mm, "end": v(-13.3, -10.1) * mm});
            skArc(sketch, "E172.0.4", {"start": v(-13.3, -10.1) * mm, "mid": v(-13.44, -10.16) * mm, "end": v(-13.5, -10.3) * mm});
            skLineSegment(sketch, "E172.0.5", {"start": v(-13.5, -10.3) * mm, "end": v(-13.5, -12) * mm});
            skArc(sketch, "E172.0.6", {"start": v(-13.5, -12) * mm, "mid": v(-13.06, -13.06) * mm, "end": v(-12, -13.5) * mm});
            skLineSegment(sketch, "E172.0.7", {"start": v(-12, -13.5) * mm, "end": v(-10.3, -13.5) * mm});
            skLineSegment(sketch, "E173", {"start": v(15.38, 16.3) * mm, "end": v(15.38, -16.5) * mm, "construction": true});
            skArc(sketch, "E174.MirrorCS", {"start": v(26.75, 15) * mm, "mid": v(27.46, 14.7) * mm, "end": v(27.75, 14) * mm});
            skLineSegment(sketch, "E175.MirrorCS", {"start": v(27.75, 14) * mm, "end": v(27.75, 12.85) * mm});
            skArc(sketch, "E176.MirrorCS", {"start": v(27.75, 12.85) * mm, "mid": v(27.53, 12.32) * mm, "end": v(27, 12.1) * mm});
            skLineSegment(sketch, "E177.MirrorCS", {"start": v(27, 12.1) * mm, "end": v(25.55, 12.1) * mm});
            skArc(sketch, "E178.MirrorCS", {"start": v(25.55, 12.1) * mm, "mid": v(25.4, 12.16) * mm, "end": v(25.35, 12.3) * mm});
            skLineSegment(sketch, "E179.MirrorCS", {"start": v(25.35, 12.3) * mm, "end": v(25.35, 13.3) * mm});
            skArc(sketch, "E180.MirrorCS", {"start": v(25.35, 13.3) * mm, "mid": v(25.3, 13.44) * mm, "end": v(25.15, 13.5) * mm});
            skLineSegment(sketch, "E181.MirrorCS", {"start": v(25.15, 13.5) * mm, "end": v(22.9, 13.5) * mm});
            skArc(sketch, "E182.MirrorCS", {"start": v(22.9, 13.5) * mm, "mid": v(22.37, 13.28) * mm, "end": v(22.15, 12.75) * mm});
            skLineSegment(sketch, "E183.MirrorCS", {"start": v(22.15, 12.75) * mm, "end": v(22.15, 11.05) * mm});
            skArc(sketch, "E184.MirrorCS", {"start": v(22.15, 11.05) * mm, "mid": v(22.34, 10.1) * mm, "end": v(22.88, 9.28) * mm});
            skLineSegment(sketch, "E185.MirrorCS", {"start": v(22.88, 9.28) * mm, "end": v(26.33, 5.83) * mm});
            skArc(sketch, "E186.MirrorCS", {"start": v(26.33, 5.83) * mm, "mid": v(27.14, 5.3) * mm, "end": v(28.1, 5.1) * mm});
            skLineSegment(sketch, "E187.MirrorCS", {"start": v(28.1, 5.1) * mm, "end": v(30.75, 5.1) * mm});
            skLineSegment(sketch, "E188.MirrorCS", {"start": v(30.75, 5.1) * mm, "end": v(33.4, 5.1) * mm});
            skArc(sketch, "E189.MirrorCS", {"start": v(33.4, 5.1) * mm, "mid": v(34.36, 5.3) * mm, "end": v(35.17, 5.83) * mm});
            skLineSegment(sketch, "E190.MirrorCS", {"start": v(35.17, 5.83) * mm, "end": v(38.62, 9.28) * mm});
            skArc(sketch, "E191.MirrorCS", {"start": v(38.62, 9.28) * mm, "mid": v(39.16, 10.1) * mm, "end": v(39.35, 11.05) * mm});
            skLineSegment(sketch, "E192.MirrorCS", {"start": v(39.35, 11.05) * mm, "end": v(39.35, 12.75) * mm});
            skArc(sketch, "E193.MirrorCS", {"start": v(39.35, 12.75) * mm, "mid": v(39.13, 13.28) * mm, "end": v(38.6, 13.5) * mm});
            skLineSegment(sketch, "E194.MirrorCS", {"start": v(38.6, 13.5) * mm, "end": v(36.35, 13.5) * mm});
            skArc(sketch, "E195.MirrorCS", {"start": v(36.35, 13.5) * mm, "mid": v(36.2, 13.44) * mm, "end": v(36.15, 13.3) * mm});
            skLineSegment(sketch, "E196.MirrorCS", {"start": v(36.15, 13.3) * mm, "end": v(36.15, 12.3) * mm});
            skArc(sketch, "E197.MirrorCS", {"start": v(36.15, 12.3) * mm, "mid": v(36.1, 12.16) * mm, "end": v(35.95, 12.1) * mm});
            skLineSegment(sketch, "E198.MirrorCS", {"start": v(35.95, 12.1) * mm, "end": v(34.5, 12.1) * mm});
            skArc(sketch, "E199.MirrorCS", {"start": v(34.5, 12.1) * mm, "mid": v(33.97, 12.32) * mm, "end": v(33.75, 12.85) * mm});
            skLineSegment(sketch, "E200.MirrorCS", {"start": v(33.75, 12.85) * mm, "end": v(33.75, 14) * mm});
            skArc(sketch, "E201.MirrorCS", {"start": v(33.75, 14) * mm, "mid": v(34.04, 14.7) * mm, "end": v(34.75, 15) * mm});
            skLineSegment(sketch, "E202.MirrorCS", {"start": v(34.75, 15) * mm, "end": v(42.75, 15) * mm});
            skArc(sketch, "E203.MirrorCS", {"start": v(42.75, 15) * mm, "mid": v(44.87, 14.12) * mm, "end": v(45.75, 12) * mm});
            skLineSegment(sketch, "E204.MirrorCS", {"start": v(45.75, 12) * mm, "end": v(45.75, 4) * mm});
            skArc(sketch, "E205.MirrorCS", {"start": v(42.75, 13.5) * mm, "mid": v(43.81, 13.06) * mm, "end": v(44.25, 12) * mm});
            skLineSegment(sketch, "E206.MirrorCS", {"start": v(41.05, 13.5) * mm, "end": v(42.75, 13.5) * mm});
            skArc(sketch, "E207.MirrorCS", {"start": v(40.85, 13.3) * mm, "mid": v(40.9, 13.44) * mm, "end": v(41.05, 13.5) * mm});
            skLineSegment(sketch, "E208.MirrorCS", {"start": v(40.85, 10.3) * mm, "end": v(40.85, 13.3) * mm});
            skArc(sketch, "E209.MirrorCS", {"start": v(41.05, 10.1) * mm, "mid": v(40.9, 10.16) * mm, "end": v(40.85, 10.3) * mm});
            skLineSegment(sketch, "E210.MirrorCS", {"start": v(44.05, 10.1) * mm, "end": v(41.05, 10.1) * mm});
            skArc(sketch, "E211.MirrorCS", {"start": v(44.25, 10.3) * mm, "mid": v(44.2, 10.16) * mm, "end": v(44.05, 10.1) * mm});
            skLineSegment(sketch, "E212.MirrorCS", {"start": v(44.25, 12) * mm, "end": v(44.25, 10.3) * mm});
            skArc(sketch, "E213.MirrorCS", {"start": v(45.75, 4) * mm, "mid": v(45.46, 3.3) * mm, "end": v(44.75, 3) * mm});
            skLineSegment(sketch, "E214.MirrorCS", {"start": v(44.75, 3) * mm, "end": v(43.6, 3) * mm});
            skArc(sketch, "E215.MirrorCS", {"start": v(43.6, 3) * mm, "mid": v(43.07, 3.22) * mm, "end": v(42.85, 3.75) * mm});
            skLineSegment(sketch, "E216.MirrorCS", {"start": v(42.85, 3.75) * mm, "end": v(42.85, 5.2) * mm});
            skArc(sketch, "E217.MirrorCS", {"start": v(42.85, 5.2) * mm, "mid": v(42.9, 5.34) * mm, "end": v(43.05, 5.4) * mm});
            skLineSegment(sketch, "E218.MirrorCS", {"start": v(43.05, 5.4) * mm, "end": v(44.05, 5.4) * mm});
            skArc(sketch, "E219.MirrorCS", {"start": v(44.05, 5.4) * mm, "mid": v(44.2, 5.46) * mm, "end": v(44.25, 5.6) * mm});
            skLineSegment(sketch, "E220.MirrorCS", {"start": v(44.25, 5.6) * mm, "end": v(44.25, 7.85) * mm});
            skArc(sketch, "E221.MirrorCS", {"start": v(44.25, 7.85) * mm, "mid": v(44.03, 8.38) * mm, "end": v(43.5, 8.6) * mm});
            skLineSegment(sketch, "E222.MirrorCS", {"start": v(43.5, 8.6) * mm, "end": v(41.8, 8.6) * mm});
            skArc(sketch, "E223.MirrorCS", {"start": v(41.8, 8.6) * mm, "mid": v(40.84, 8.4) * mm, "end": v(40.03, 7.87) * mm});
            skLineSegment(sketch, "E224.MirrorCS", {"start": v(40.03, 7.87) * mm, "end": v(36.58, 4.42) * mm});
            skArc(sketch, "E225.MirrorCS", {"start": v(36.58, 4.42) * mm, "mid": v(36.04, 3.6) * mm, "end": v(35.85, 2.65) * mm});
            skLineSegment(sketch, "E226.MirrorCS", {"start": v(35.85, 2.65) * mm, "end": v(35.85, 0) * mm});
            skLineSegment(sketch, "E227.MirrorCS", {"start": v(35.85, 0) * mm, "end": v(35.85, -2.65) * mm});
            skArc(sketch, "E228.MirrorCS", {"start": v(35.85, -2.65) * mm, "mid": v(36.04, -3.6) * mm, "end": v(36.58, -4.42) * mm});
            skLineSegment(sketch, "E229.MirrorCS", {"start": v(36.58, -4.42) * mm, "end": v(40.03, -7.87) * mm});
            skArc(sketch, "E230.MirrorCS", {"start": v(40.03, -7.87) * mm, "mid": v(40.84, -8.4) * mm, "end": v(41.8, -8.6) * mm});
            skLineSegment(sketch, "E231.MirrorCS", {"start": v(41.8, -8.6) * mm, "end": v(43.5, -8.6) * mm});
            skArc(sketch, "E232.MirrorCS", {"start": v(43.5, -8.6) * mm, "mid": v(44.03, -8.38) * mm, "end": v(44.25, -7.85) * mm});
            skLineSegment(sketch, "E233.MirrorCS", {"start": v(44.25, -7.85) * mm, "end": v(44.25, -5.6) * mm});
            skArc(sketch, "E234.MirrorCS", {"start": v(44.25, -5.6) * mm, "mid": v(44.2, -5.46) * mm, "end": v(44.05, -5.4) * mm});
            skLineSegment(sketch, "E235.MirrorCS", {"start": v(44.05, -5.4) * mm, "end": v(43.05, -5.4) * mm});
            skArc(sketch, "E236.MirrorCS", {"start": v(43.05, -5.4) * mm, "mid": v(42.9, -5.34) * mm, "end": v(42.85, -5.2) * mm});
            skLineSegment(sketch, "E237.MirrorCS", {"start": v(42.85, -5.2) * mm, "end": v(42.85, -3.75) * mm});
            skArc(sketch, "E238.MirrorCS", {"start": v(42.85, -3.75) * mm, "mid": v(43.07, -3.22) * mm, "end": v(43.6, -3) * mm});
            skLineSegment(sketch, "E239.MirrorCS", {"start": v(43.6, -3) * mm, "end": v(44.75, -3) * mm});
            skArc(sketch, "E240.MirrorCS", {"start": v(44.75, -3) * mm, "mid": v(45.46, -3.3) * mm, "end": v(45.75, -4) * mm});
            skLineSegment(sketch, "E241.MirrorCS", {"start": v(45.75, -4) * mm, "end": v(45.75, -12) * mm});
            skArc(sketch, "E242.MirrorCS", {"start": v(45.75, -12) * mm, "mid": v(44.87, -14.12) * mm, "end": v(42.75, -15) * mm});
            skLineSegment(sketch, "E243.MirrorCS", {"start": v(44.25, -10.3) * mm, "end": v(44.25, -12) * mm});
            skArc(sketch, "E244.MirrorCS", {"start": v(44.25, -12) * mm, "mid": v(43.81, -13.06) * mm, "end": v(42.75, -13.5) * mm});
            skLineSegment(sketch, "E245.MirrorCS", {"start": v(42.75, -13.5) * mm, "end": v(41.05, -13.5) * mm});
            skArc(sketch, "E246.MirrorCS", {"start": v(41.05, -13.5) * mm, "mid": v(40.9, -13.44) * mm, "end": v(40.85, -13.3) * mm});
            skLineSegment(sketch, "E247.MirrorCS", {"start": v(40.85, -13.3) * mm, "end": v(40.85, -10.3) * mm});
            skArc(sketch, "E248.MirrorCS", {"start": v(40.85, -10.3) * mm, "mid": v(40.9, -10.16) * mm, "end": v(41.05, -10.1) * mm});
            skLineSegment(sketch, "E249.MirrorCS", {"start": v(41.05, -10.1) * mm, "end": v(44.05, -10.1) * mm});
            skArc(sketch, "E250.MirrorCS", {"start": v(44.05, -10.1) * mm, "mid": v(44.2, -10.16) * mm, "end": v(44.25, -10.3) * mm});
            skLineSegment(sketch, "E251.MirrorCS", {"start": v(42.75, -15) * mm, "end": v(34.75, -15) * mm});
            skArc(sketch, "E252.MirrorCS", {"start": v(34.75, -15) * mm, "mid": v(34.04, -14.7) * mm, "end": v(33.75, -14) * mm});
            skLineSegment(sketch, "E253.MirrorCS", {"start": v(33.75, -14) * mm, "end": v(33.75, -12.85) * mm});
            skArc(sketch, "E254.MirrorCS", {"start": v(33.75, -12.85) * mm, "mid": v(33.97, -12.32) * mm, "end": v(34.5, -12.1) * mm});
            skLineSegment(sketch, "E255.MirrorCS", {"start": v(34.5, -12.1) * mm, "end": v(35.95, -12.1) * mm});
            skArc(sketch, "E256.MirrorCS", {"start": v(35.95, -12.1) * mm, "mid": v(36.1, -12.16) * mm, "end": v(36.15, -12.3) * mm});
            skLineSegment(sketch, "E257.MirrorCS", {"start": v(36.15, -12.3) * mm, "end": v(36.15, -13.3) * mm});
            skArc(sketch, "E258.MirrorCS", {"start": v(36.15, -13.3) * mm, "mid": v(36.2, -13.44) * mm, "end": v(36.35, -13.5) * mm});
            skLineSegment(sketch, "E259.MirrorCS", {"start": v(36.35, -13.5) * mm, "end": v(38.6, -13.5) * mm});
            skArc(sketch, "E260.MirrorCS", {"start": v(38.6, -13.5) * mm, "mid": v(39.13, -13.28) * mm, "end": v(39.35, -12.75) * mm});
            skLineSegment(sketch, "E261.MirrorCS", {"start": v(39.35, -12.75) * mm, "end": v(39.35, -11.05) * mm});
            skArc(sketch, "E262.MirrorCS", {"start": v(39.35, -11.05) * mm, "mid": v(39.16, -10.1) * mm, "end": v(38.62, -9.28) * mm});
            skLineSegment(sketch, "E263.MirrorCS", {"start": v(38.62, -9.28) * mm, "end": v(35.17, -5.83) * mm});
            skArc(sketch, "E264.MirrorCS", {"start": v(35.17, -5.83) * mm, "mid": v(34.36, -5.3) * mm, "end": v(33.4, -5.1) * mm});
            skLineSegment(sketch, "E265.MirrorCS", {"start": v(33.4, -5.1) * mm, "end": v(30.75, -5.1) * mm});
            skLineSegment(sketch, "E266.MirrorCS", {"start": v(30.75, -5.1) * mm, "end": v(28.1, -5.1) * mm});
            skArc(sketch, "E267.MirrorCS", {"start": v(28.1, -5.1) * mm, "mid": v(27.14, -5.3) * mm, "end": v(26.33, -5.83) * mm});
            skLineSegment(sketch, "E268.MirrorCS", {"start": v(26.33, -5.83) * mm, "end": v(22.88, -9.28) * mm});
            skArc(sketch, "E269.MirrorCS", {"start": v(22.88, -9.28) * mm, "mid": v(22.34, -10.1) * mm, "end": v(22.15, -11.05) * mm});
            skLineSegment(sketch, "E270.MirrorCS", {"start": v(22.15, -11.05) * mm, "end": v(22.15, -12.75) * mm});
            skArc(sketch, "E271.MirrorCS", {"start": v(22.15, -12.75) * mm, "mid": v(22.37, -13.28) * mm, "end": v(22.9, -13.5) * mm});
            skLineSegment(sketch, "E272.MirrorCS", {"start": v(22.9, -13.5) * mm, "end": v(25.15, -13.5) * mm});
            skArc(sketch, "E273.MirrorCS", {"start": v(25.15, -13.5) * mm, "mid": v(25.3, -13.44) * mm, "end": v(25.35, -13.3) * mm});
            skLineSegment(sketch, "E274.MirrorCS", {"start": v(25.35, -13.3) * mm, "end": v(25.35, -12.3) * mm});
            skArc(sketch, "E275.MirrorCS", {"start": v(25.35, -12.3) * mm, "mid": v(25.4, -12.16) * mm, "end": v(25.55, -12.1) * mm});
            skLineSegment(sketch, "E276.MirrorCS", {"start": v(25.55, -12.1) * mm, "end": v(27, -12.1) * mm});
            skArc(sketch, "E277.MirrorCS", {"start": v(27, -12.1) * mm, "mid": v(27.53, -12.32) * mm, "end": v(27.75, -12.85) * mm});
            skLineSegment(sketch, "E278.MirrorCS", {"start": v(27.75, -12.85) * mm, "end": v(27.75, -14) * mm});
            skArc(sketch, "E279.MirrorCS", {"start": v(27.75, -14) * mm, "mid": v(27.46, -14.7) * mm, "end": v(26.75, -15) * mm});
            skCircle(sketch, "E280.MirrorC", {"center": v(30.75, 0) * mm, "radius": 2.45 * mm});
            skLineSegment(sketch, "E281.MirrorCS", {"start": v(24.92, 4.42) * mm, "end": v(21.47, 7.87) * mm});
            skArc(sketch, "E282.MirrorCS", {"start": v(25.65, 2.65) * mm, "mid": v(25.46, 3.6) * mm, "end": v(24.92, 4.42) * mm});
            skLineSegment(sketch, "E283.MirrorCS", {"start": v(25.65, 0) * mm, "end": v(25.65, 2.65) * mm});
            skLineSegment(sketch, "E284.MirrorCS", {"start": v(25.65, -2.65) * mm, "end": v(25.65, 0) * mm});
            skArc(sketch, "E285.MirrorCS", {"start": v(24.92, -4.42) * mm, "mid": v(25.46, -3.6) * mm, "end": v(25.65, -2.65) * mm});
            skLineSegment(sketch, "E286.MirrorCS", {"start": v(21.47, -7.87) * mm, "end": v(24.92, -4.42) * mm});
            skLineSegment(sketch, "E287", {"start": v(4, 15) * mm, "end": v(26.75, 15) * mm});
            skLineSegment(sketch, "E288", {"start": v(4, -15) * mm, "end": v(26.75, -15) * mm});
            skLineSegment(sketch, "E289", {"start": v(12.12, 12.75) * mm, "end": v(18.63, 12.75) * mm});
            skLineSegment(sketch, "E290", {"start": v(10.62, 9.83) * mm, "end": v(10.62, 11.25) * mm});
            skLineSegment(sketch, "E291.MirrorCS", {"start": v(20.13, 9.83) * mm, "end": v(20.13, 11.25) * mm});
            skLineSegment(sketch, "E292", {"start": v(5.83, 4.42) * mm, "end": v(10.19, 8.77) * mm});
            skLineSegment(sketch, "E293", {"start": v(24.92, 4.42) * mm, "end": v(20.56, 8.77) * mm});
            skPoint(sketch, "E294.visualSharp", {"position": v(10.62, 12.75) * mm});
            skArc(sketch, "E294.filletArc", {"start": v(12.12, 12.75) * mm, "mid": v(11.06, 12.31) * mm, "end": v(10.62, 11.25) * mm});
            skPoint(sketch, "E295.visualSharp", {"position": v(20.13, 12.75) * mm});
            skArc(sketch, "E295.filletArc", {"start": v(20.13, 11.25) * mm, "mid": v(19.69, 12.31) * mm, "end": v(18.63, 12.75) * mm});
            skPoint(sketch, "E296.newPointA", {"position": v(10.62, 9.18) * mm});
            skArc(sketch, "E296.filletArc", {"start": v(10.19, 8.77) * mm, "mid": v(10.51, 9.26) * mm, "end": v(10.62, 9.83) * mm});
            skPoint(sketch, "E297.newPointA", {"position": v(20.13, 9.18) * mm});
            skArc(sketch, "E297.filletArc", {"start": v(20.13, 9.83) * mm, "mid": v(20.24, 9.26) * mm, "end": v(20.56, 8.77) * mm});
            skLineSegment(sketch, "E298.MirrorCS", {"start": v(5.83, -4.42) * mm, "end": v(10.19, -8.77) * mm});
            skArc(sketch, "E299.MirrorCS", {"start": v(10.19, -8.77) * mm, "mid": v(10.51, -9.26) * mm, "end": v(10.62, -9.83) * mm});
            skLineSegment(sketch, "E300.MirrorCS", {"start": v(10.62, -9.83) * mm, "end": v(10.62, -11.25) * mm});
            skArc(sketch, "E301.MirrorCS", {"start": v(12.12, -12.75) * mm, "mid": v(11.06, -12.31) * mm, "end": v(10.62, -11.25) * mm});
            skLineSegment(sketch, "E302.MirrorCS", {"start": v(12.12, -12.75) * mm, "end": v(18.63, -12.75) * mm});
            skArc(sketch, "E303.MirrorCS", {"start": v(20.13, -11.25) * mm, "mid": v(19.69, -12.31) * mm, "end": v(18.63, -12.75) * mm});
            skLineSegment(sketch, "E304.MirrorCS", {"start": v(20.13, -9.83) * mm, "end": v(20.13, -11.25) * mm});
            skArc(sketch, "E305.MirrorCS", {"start": v(20.13, -9.83) * mm, "mid": v(20.24, -9.26) * mm, "end": v(20.56, -8.77) * mm});
            skLineSegment(sketch, "E306.MirrorCS", {"start": v(24.92, -4.42) * mm, "end": v(20.56, -8.77) * mm});
            skSolve(sketch);
        }
        {
            var Q0;
            Q0=makeQuery(id+"F2.imprint","IMPRINT",FACE,{"disambiguationData":[TD([[makeQuery(id+"F2.imprint","IMPRINT",EDGE,{"derivedFrom":sQuery(id+"F2.wireOp",EDGE,"E169.0")}),-1.0]])]});
            extrude(context, id + "F3", {"entities" : qUnion([Q0]), "depth" : 300 * mm});
        }
    });
